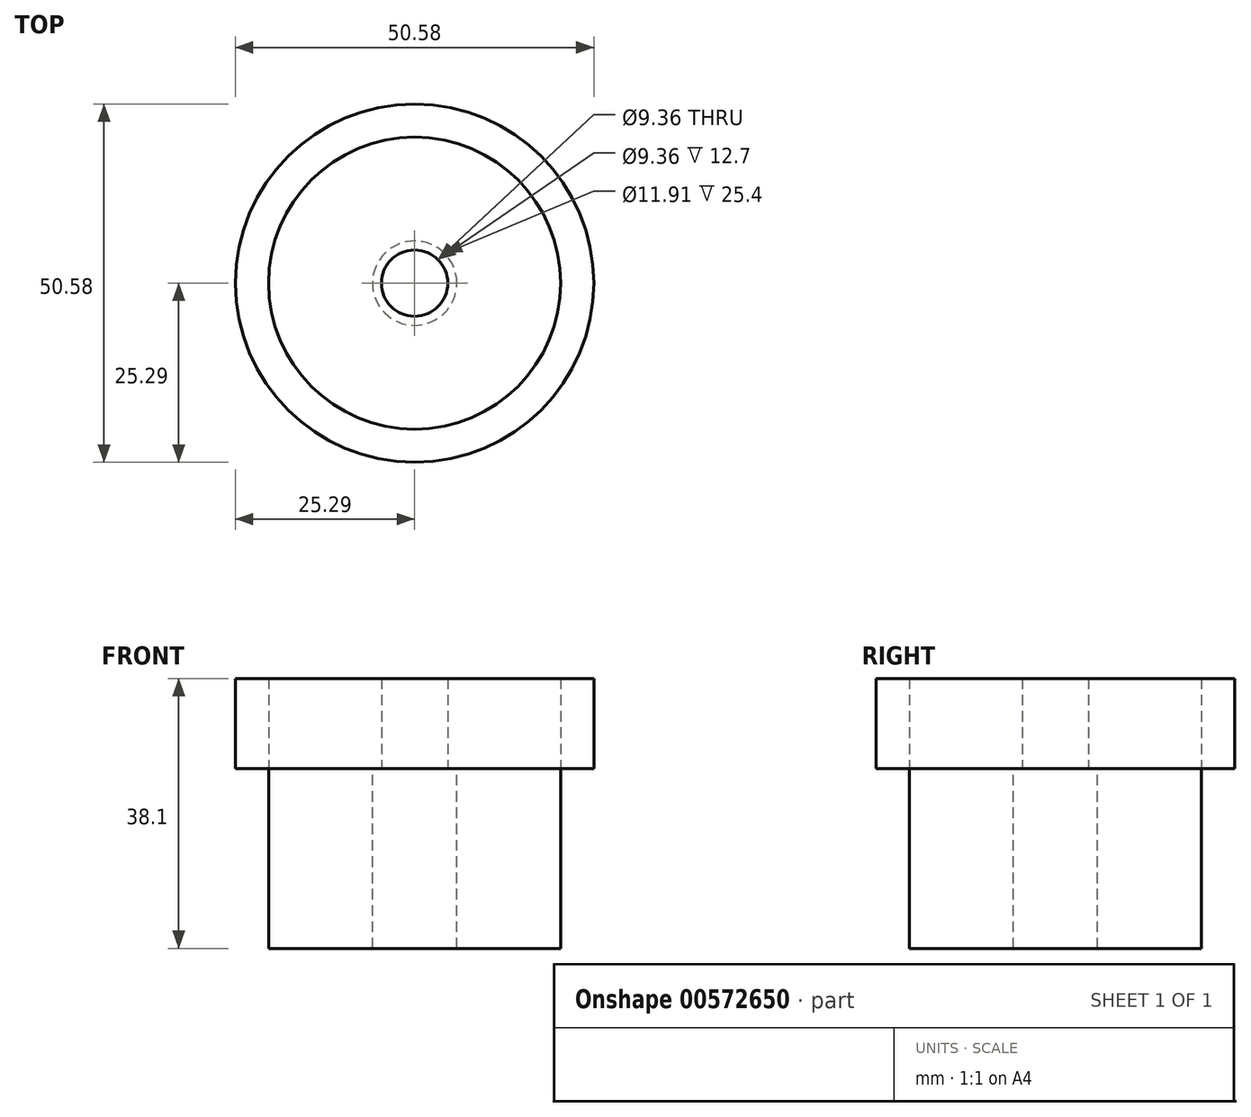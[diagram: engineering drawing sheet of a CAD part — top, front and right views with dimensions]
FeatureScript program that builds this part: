
annotation { "Feature Type Name" : "Feature", "Feature Type Description" : "" }
export const myFeature = defineFeature(function(context is Context, id is Id, definition is map)
    precondition{}
    {
        {
            var Q0;
            Q0=qCreatedBy(makeId("Top.planeOp"),FACE);
            var sketch = newSketch(context, id + "F0", { "sketchPlane" : qUnion([Q0])});
            skCircle(sketch, "E0", {"center": v(0, 0) * mm, "radius": 25.29 * mm});
            skCircle(sketch, "E1", {"center": v(0, 0) * mm, "radius": 25.27 * mm});
            skCircle(sketch, "E2", {"center": v(-113.97, 15.37) * mm, "radius": 25.18 * mm});
            skSolve(sketch);
        }
        {
            var Q0;
            Q0=qCreatedBy(makeId("Top.planeOp"),FACE);
            var sketch = newSketch(context, id + "F1", { "sketchPlane" : qUnion([Q0])});
            skCircle(sketch, "E3", {"center": v(0, 0) * mm, "radius": 20.61 * mm});
            skCircle(sketch, "E4", {"center": v(0, 0) * mm, "radius": 4.68 * mm});
            skSolve(sketch);
        }
        {
            var Q0;
            Q0=makeQuery(id+"F0.imprint","IMPRINT",FACE,{"disambiguationData":[TD([[makeQuery(id+"F0.imprint","IMPRINT",EDGE,{"derivedFrom":sQuery(id+"F0.wireOp",EDGE,"E0")}),1.0]])]});
            var Q1;
            {var subQ0=sQuery(id+"F0.wireOp",EDGE,"E2");var subQ1=sQuery(id+"F0.wireOp",EDGE,"E1");var subQ2=makeQuery(id+"F0.imprint","INTERSECT",VERTEX,{"disambiguationData":[OD(0.0)],"derivedFrom":[subQ1,subQ0]});Q1=makeQuery(id+"F0.imprint","IMPRINT",FACE,{"disambiguationData":[TD([[makeQuery(id+"F0.imprint","IMPRINT",EDGE,{"disambiguationData":[TD([[subQ2,1.0]])],"derivedFrom":subQ1}),1.0]])]});}
            var Q2;
            Q2=makeQuery(id+"F0.imprint","IMPRINT",FACE,{"disambiguationData":[TD([[makeQuery(id+"F0.imprint","IMPRINT",EDGE,{"derivedFrom":sQuery(id+"F0.wireOp",EDGE,"E1")}),1.0]])]});
            var Q3;
            Q3 = qSketchRegion(id + "F1", true);
            extrude(context, id + "F2", {"entities" : qUnion([Q0, Q1, Q2, Q3]), "depth" : 12.7 * mm, "offsetDistance" : 25.4 * mm});
        }
        {
            var Q0;
            Q0=makeQuery(id+"F2.opExtrude","CAP_FACE",FACE,{"disambiguationData":[OSD([sQuery(id+"F1.wireOp",EDGE,"E3")])],"isStart":false});
            extrude(context, id + "F3", {"entities" : qUnion([Q0]), "oppositeDirection" : true, "depth" : 38.1 * mm, "offsetDistance" : 25.4 * mm});
        }
        {
            var Q0;
            Q0=qCreatedBy(makeId("Top.planeOp"),FACE);
            var sketch = newSketch(context, id + "F4", { "sketchPlane" : qUnion([Q0])});
            skCircle(sketch, "E5", {"center": v(0, 0) * mm, "radius": 5.95 * mm});
            skSolve(sketch);
        }
        {
            var Q0;
            Q0 = qSketchRegion(id + "F4", true);
            var Q1;
            Q1=makeQuery(id+"F3.opExtrude","CAP_FACE",FACE,{"disambiguationData":[OSD([sQuery(id+"F1.wireOp",EDGE,"E3"),sQuery(id+"F1.wireOp",EDGE,"E4")])],"isStart":false});
            extrude(context, id + "F5", {"entities" : qUnion([Q0, Q1]), "operationType" : NewBodyOperationType.REMOVE, "depth" : -38.1 * mm, "offsetDistance" : 25.4 * mm});
        }
    });
